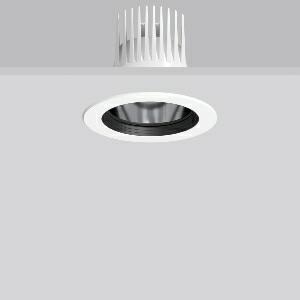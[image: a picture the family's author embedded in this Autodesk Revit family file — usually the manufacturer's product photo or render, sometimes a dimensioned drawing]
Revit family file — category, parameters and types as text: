
# Revit family: heledon_maxi_e_901766_002_ace7
name_source: partatom
category: Lighting Fixtures
units: mm (PartAtom-declared; Revit-internal decimal feet)

## family parameters
Cut with Voids When Loaded = No
Host = Face
Light Source = No
Part Type = Normal
Room Calculation Point = No
Round Connector Dimension = Use Diameter
Shared = No

## types (1)
- HELEDON maxi E (1 x LED Modul 930, 4150 lm, 3000)
    Apparent Load = 35 VA
    Approval mark = CE
    CIE Flux Codes = 97 100 100 100 100
    Color Rendering = 90
    Color Temperature = 3000
    Default Elevation = 1800 mm
    Description = Series: HELEDON maxi
Round recessed downlight. Housing: die-cast aluminium, powder-coated. Black plastic ring and recessed LED to prevent glare from the side. Optical assembly with reflector made of MIRO-Silver with 98% total light reflection for outstanding efficiency - can be changed without tools. Best colour rendering index Ra>90. Suitable for Recessed ceiling mounting. Installation without tools thanks to spring fastening system. Including separate LED converter with connecting cable 600 mm.High quality converter without flickering and stroboscopic effect. Through-wiring box (5 pole) available as accessory. The following accessories can be mounted without use of tools: interchangeable lenses, decorative glasses, honeycomb louvre, clear and frosted diffusers, white interchangeable plastic ring. 
Colour: traffic white, matt (RAL 9016)
Diameter: 162 mm
Height: 3 mm
Cut-out diameter: 152 mm
Recess height: 200 mm
Luminaire: recess height: 135 mm
Lamp: LED
Socket: without socket
Colour temperature: 3000K
Colour rendering index (CRI): 92
System power: 35 W
Rated luminous flux: 4150 lm
Luminous efficiency: 119 lm/W
Control gear: Regulated power supply
Protection class: II
Type of protection: IP 20
    Height = 0 mm  [stored 0 ft]
    Lamp = 1 x LED Modul 930
    Lamp Light Flux = 4150 lm
    Lamp count = 1
    Length = 162 mm
    Lifetime = 50000 h
    Luminous efficacy = 119 lm/W
    Manufacturer = RZB
    ModVariant = No
    Model = 901766.002
    Mounting Place = Ceiling
    Mounting Type = Recessed
    Number of Poles = 1
    OnlyDefault = Yes
    Power Factor = 1
    Product Name = HELEDON maxi E
    Product group = Recessed downlights
    ProductGroupID = 402
    Protection Class = Protection class II
    Protection Degree = IP 20
    RLX_Detail_Level = 1
    RLX_Emergency_Light_Flux = 0 lm
    RLX_Emergency_Type = 0
    RLX_Emergency_Type_DB = No
    RlxData = <blob elided: 118629 chars, md5=5aeca2f6>
    Socket = socket
    Standby Power = 0 W
    System Light Flux = 4150 lm
    System Power = 35 W
    Type Comments = Product without accessories
    Type Image = 901662.002.jpg
    URL = http://relux.com
    VarID = ---
    Voltage = 230 V
    Voltage Range = 220-240 V
    Weight = 0.00 kg
    Width = 0 mm  [stored 0 ft]

note: [stored X ft] marks values corroborated as IEEE doubles in the binary element streams (Revit-internal decimal feet)

## geometry (parser evidence)
native form markers: Blend x4, Sweep x12
no freeform markers — native parametric forms only
